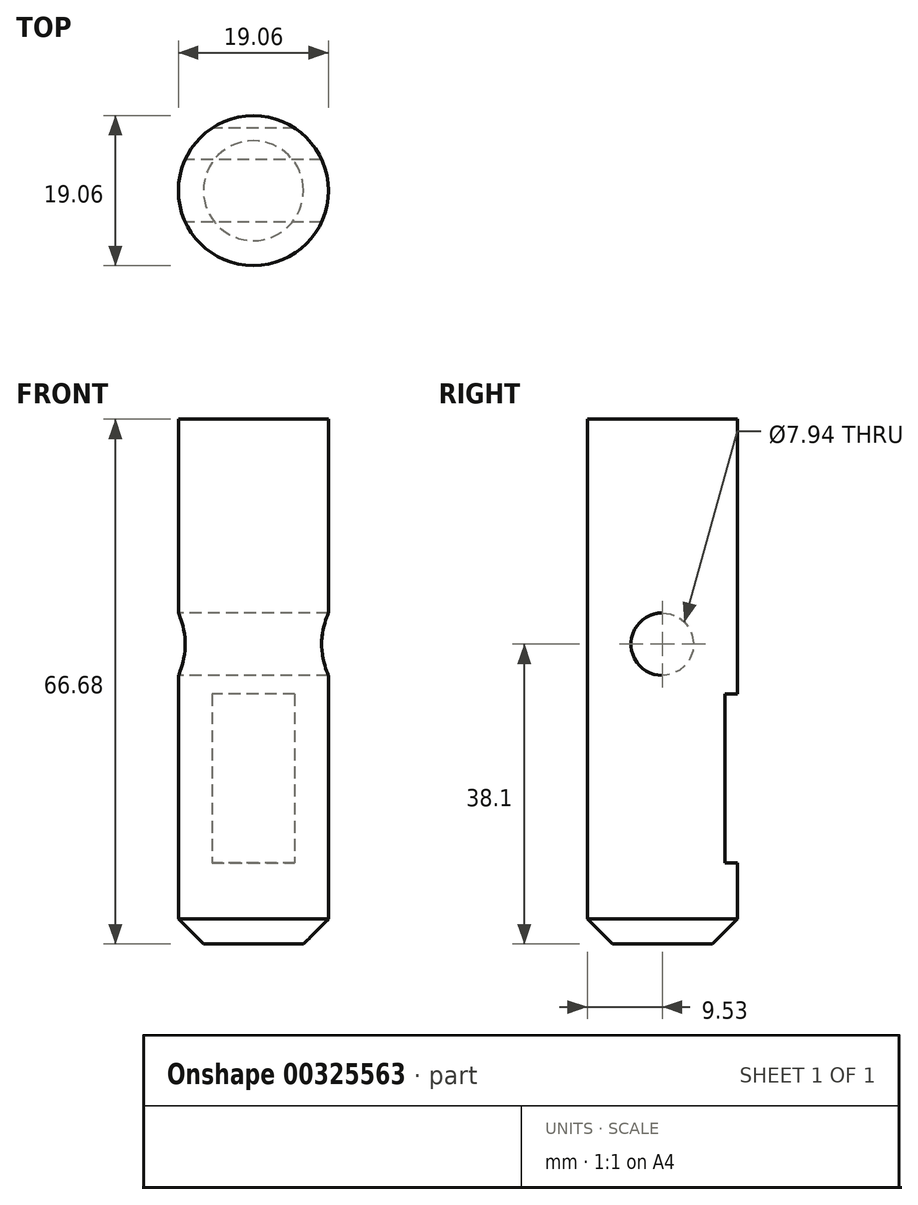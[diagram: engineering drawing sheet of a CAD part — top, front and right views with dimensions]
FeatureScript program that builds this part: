
annotation { "Feature Type Name" : "Feature", "Feature Type Description" : "" }
export const myFeature = defineFeature(function(context is Context, id is Id, definition is map)
    precondition{}
    {
        {
            var Q0;
            Q0=qCreatedBy(makeId("Top.planeOp"),FACE);
            var sketch = newSketch(context, id + "F0", { "sketchPlane" : qUnion([Q0])});
            skCircle(sketch, "E0", {"center": v(0, 0) * mm, "radius": 9.53 * mm});
            skSolve(sketch);
        }
        {
            var Q0;
            Q0=makeQuery(id+"F0.imprint","IMPRINT",FACE,{"disambiguationData":[TD([[makeQuery(id+"F0.imprint","IMPRINT",EDGE,{"derivedFrom":sQuery(id+"F0.wireOp",EDGE,"E0")}),1.0]])]});
            extrude(context, id + "F1", {"entities" : qUnion([Q0]), "depth" : 66.67 * mm});
        }
        {
            var Q0;
            Q0=makeQuery(id+"F1.opExtrude","CAP_EDGE",EDGE,{"disambiguationData":[OSD([sQuery(id+"F0.wireOp",EDGE,"E0")])],"isStart":true});
            chamfer(context, id + "F2", {"entities" : qUnion([Q0]), "width" : 3.17 * mm, "tangentPropagation" : true});
        }
        {
            var Q0;
            Q0=qCreatedBy(makeId("Right.planeOp"),FACE);
            var sketch = newSketch(context, id + "F3", { "sketchPlane" : qUnion([Q0])});
            skLineSegment(sketch, "E1", {"start": v(7.94, 10.32) * mm, "end": v(7.94, 31.75) * mm});
            skLineSegment(sketch, "E2", {"start": v(7.94, 31.75) * mm, "end": v(42.7, 31.75) * mm});
            skLineSegment(sketch, "E3", {"start": v(42.7, 31.75) * mm, "end": v(42.7, 10.32) * mm});
            skLineSegment(sketch, "E4", {"start": v(42.7, 10.32) * mm, "end": v(7.94, 10.32) * mm});
            skLineSegment(sketch, "E5", {"start": v(9.53, 38.16) * mm, "end": v(9.53, 0) * mm});
            skLineSegment(sketch, "E6", {"start": v(4.75, 38.16) * mm, "end": v(4.75, 0) * mm});
            skCircle(sketch, "E7", {"center": v(0, 38.1) * mm, "radius": 3.97 * mm});
            skSolve(sketch);
        }
        {
            var Q0;
            {var subQ0=sQuery(id+"F3.wireOp",EDGE,"E3");Q0=makeQuery(id+"F3.imprint","IMPRINT",FACE,{"disambiguationData":[TD([[makeQuery(id+"F3.imprint","IMPRINT",EDGE,{"derivedFrom":subQ0}),-1.0]])]});}
            var Q1;
            {var subQ0=sQuery(id+"F3.wireOp",EDGE,"E1");Q1=makeQuery(id+"F3.imprint","IMPRINT",FACE,{"disambiguationData":[TD([[makeQuery(id+"F3.imprint","IMPRINT",EDGE,{"derivedFrom":subQ0}),-1.0]])]});}
            var Q2;
            Q2=makeQuery(id+"F3.imprint","IMPRINT",FACE,{"disambiguationData":[TD([[makeQuery(id+"F3.imprint","IMPRINT",EDGE,{"derivedFrom":sQuery(id+"F3.wireOp",EDGE,"E7")}),1.0]])]});
            extrude(context, id + "F4", {"entities" : qUnion([Q0, Q1, Q2]), "operationType" : NewBodyOperationType.REMOVE, "endBound" : BoundingType.SYMMETRIC, "depth" : 81.68 * mm});
        }
    });
